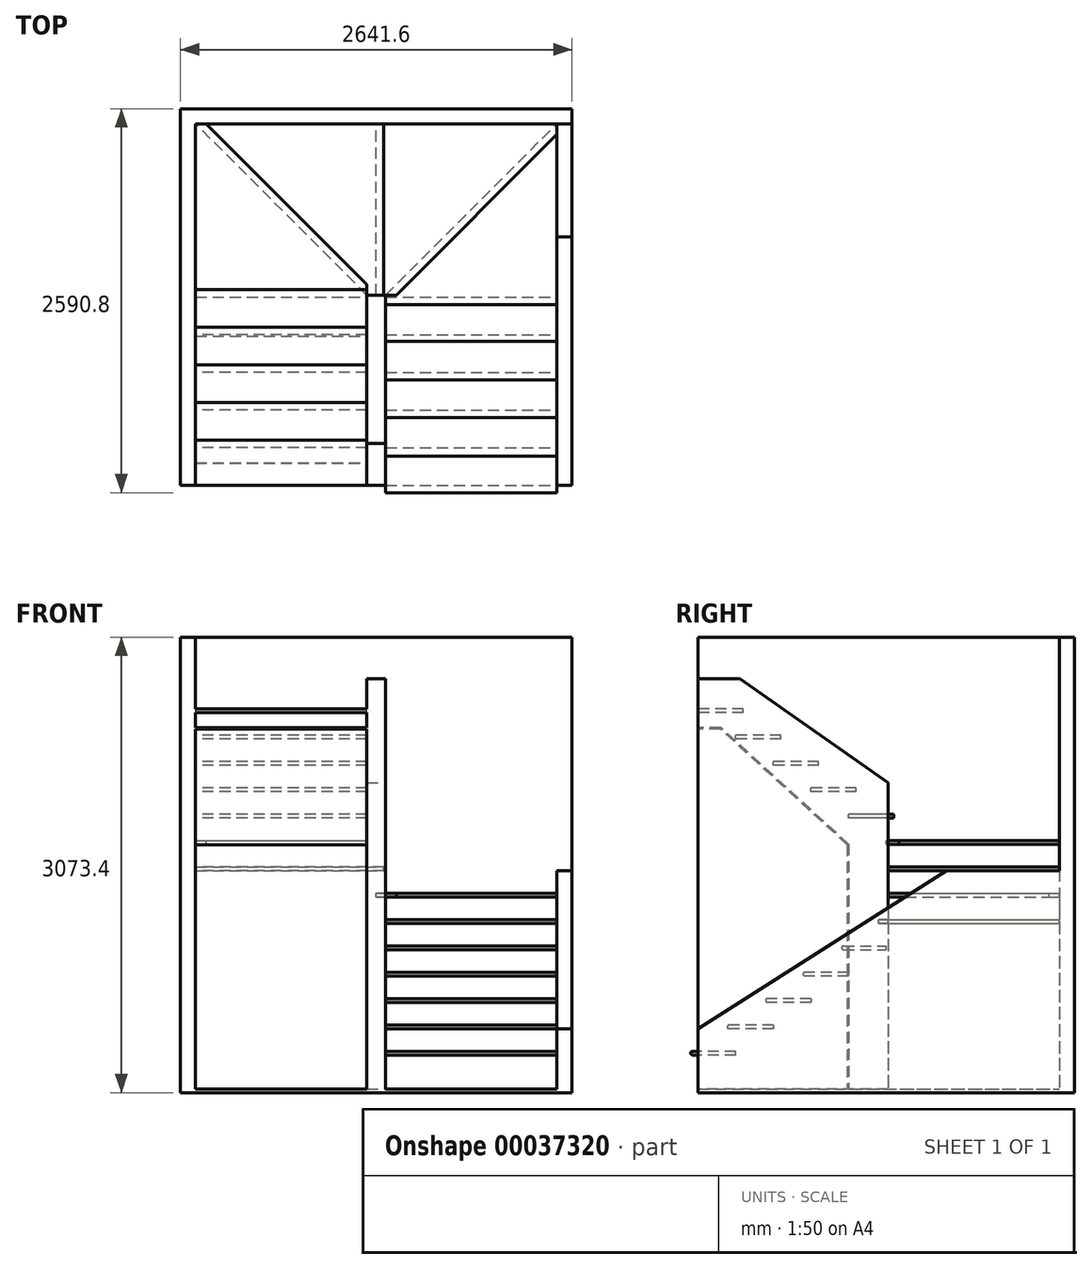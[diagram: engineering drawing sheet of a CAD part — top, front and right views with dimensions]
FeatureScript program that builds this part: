
annotation { "Feature Type Name" : "Feature", "Feature Type Description" : "" }
export const myFeature = defineFeature(function(context is Context, id is Id, definition is map)
    precondition{}
    {
        {
            var Q0;
            Q0=qCreatedBy(makeId("Top.planeOp"),FACE);
            var sketch = newSketch(context, id + "F0", { "sketchPlane" : qUnion([Q0])});
            skLineSegment(sketch, "E0.bottom", {"start": v(-1219.2, 0) * mm, "end": v(-63.5, 0) * mm});
            skLineSegment(sketch, "E0.top", {"start": v(-1219.2, 2438.4) * mm, "end": v(1219.2, 2438.4) * mm});
            skLineSegment(sketch, "E0.left", {"start": v(-1219.2, 0) * mm, "end": v(-1219.2, 2438.4) * mm});
            skLineSegment(sketch, "E0.right", {"start": v(1219.2, 0) * mm, "end": v(1219.2, 2438.4) * mm});
            skLineSegment(sketch, "E1", {"start": v(-63.5, 0) * mm, "end": v(-63.5, 1282.7) * mm});
            skLineSegment(sketch, "E2", {"start": v(-63.5, 1282.7) * mm, "end": v(63.5, 1282.7) * mm});
            skLineSegment(sketch, "E3", {"start": v(63.5, 1282.7) * mm, "end": v(63.5, 0) * mm});
            skLineSegment(sketch, "E4", {"start": v(0, 1282.7) * mm, "end": v(0, 0) * mm, "construction": true});
            skLineSegment(sketch, "E5.trimOffspring", {"start": v(63.5, 0) * mm, "end": v(1219.2, 0) * mm});
            skLineSegment(sketch, "E6", {"start": v(-1219.2, 254) * mm, "end": v(-63.5, 254) * mm});
            skLineSegment(sketch, "E7", {"start": v(-1219.2, 508) * mm, "end": v(-63.5, 508) * mm});
            skLineSegment(sketch, "E8", {"start": v(-1219.2, 762) * mm, "end": v(-63.5, 762) * mm});
            skLineSegment(sketch, "E9", {"start": v(-1219.2, 1016) * mm, "end": v(-63.5, 1016) * mm});
            skLineSegment(sketch, "E10", {"start": v(0, 1282.7) * mm, "end": v(0, 2438.4) * mm});
            skLineSegment(sketch, "E11", {"start": v(63.5, 1282.7) * mm, "end": v(1219.2, 2438.4) * mm});
            skLineSegment(sketch, "E12", {"start": v(-63.5, 1282.7) * mm, "end": v(-1219.2, 2438.4) * mm});
            skLineSegment(sketch, "E13.trimOffspring", {"start": v(63.5, 762) * mm, "end": v(1219.2, 762) * mm});
            skLineSegment(sketch, "E14.trimOffspring", {"start": v(63.5, 508) * mm, "end": v(1219.2, 508) * mm});
            skLineSegment(sketch, "E15.trimOffspring", {"start": v(63.5, 254) * mm, "end": v(1219.2, 254) * mm});
            skLineSegment(sketch, "E16.trimOffspring", {"start": v(63.5, 1016) * mm, "end": v(1219.2, 1016) * mm});
            skLineSegment(sketch, "E17", {"start": v(-1219.2, 1270) * mm, "end": v(-63.5, 1270) * mm});
            skLineSegment(sketch, "E18.trimOffspring", {"start": v(63.5, 1270) * mm, "end": v(1219.2, 1270) * mm});
            skSolve(sketch);
        }
        {
            var Q0;
            Q0=qCreatedBy(makeId("Top.planeOp"),FACE);
            var sketch = newSketch(context, id + "F1", { "sketchPlane" : qUnion([Q0])});
            skLineSegment(sketch, "E19.0", {"start": v(-1219.2, 0) * mm, "end": v(-1219.2, 2438.4) * mm});
            skLineSegment(sketch, "E19.1", {"start": v(-1219.2, 2438.4) * mm, "end": v(1219.2, 2438.4) * mm});
            skLineSegment(sketch, "E19.2", {"start": v(1219.2, 0) * mm, "end": v(1219.2, 2438.4) * mm});
            skLineSegment(sketch, "E20.0", {"start": v(1320.8, 0) * mm, "end": v(1320.8, 2540) * mm});
            skLineSegment(sketch, "E20.1", {"start": v(-1320.8, 2540) * mm, "end": v(1320.8, 2540) * mm});
            skLineSegment(sketch, "E20.2", {"start": v(-1320.8, 0) * mm, "end": v(-1320.8, 2540) * mm});
            skLineSegment(sketch, "E21", {"start": v(-1320.8, 0) * mm, "end": v(-1219.2, 0) * mm});
            skLineSegment(sketch, "E22", {"start": v(1219.2, 0) * mm, "end": v(1320.8, 0) * mm});
            skSolve(sketch);
        }
        {
            var Q0;
            Q0 = qSketchRegion(id + "F1", true);
            extrude(context, id + "F2", {"entities" : qUnion([Q0]), "depth" : 3048 * mm});
        }
        {
            var Q0;
            Q0=qCreatedBy(makeId("Top.planeOp"),FACE);
            cPlane(context, id + "F3", {"entities" : qUnion([Q0]), "cplaneType" : CPlaneType.OFFSET, "offset" : 254 * mm, "width" : 152.4 * mm, "height" : 152.4 * mm});
        }
        {
            var Q0;
            Q0=qCreatedBy(id+"F3.planeOp",FACE);
            var sketch = newSketch(context, id + "F4", { "sketchPlane" : qUnion([Q0])});
            skLineSegment(sketch, "E23.bottom", {"start": v(63.5, 254) * mm, "end": v(1219.2, 254) * mm});
            skLineSegment(sketch, "E23.top", {"start": v(63.5, -50.8) * mm, "end": v(1219.2, -50.8) * mm});
            skLineSegment(sketch, "E23.left", {"start": v(63.5, 254) * mm, "end": v(63.5, -50.8) * mm});
            skLineSegment(sketch, "E23.right", {"start": v(1219.2, 254) * mm, "end": v(1219.2, -50.8) * mm});
            skSolve(sketch);
        }
        {
            var Q0;
            Q0 = qSketchRegion(id + "F4", true);
            extrude(context, id + "F5", {"entities" : qUnion([Q0]), "operationType" : NewBodyOperationType.ADD, "oppositeDirection" : true, "depth" : 25.4 * mm});
        }
        {
            var Q0;
            Q0=makeQuery(id+"F5.opExtrude","CAP_EDGE",EDGE,{"disambiguationData":[OSD([sQuery(id+"F4.wireOp",EDGE,"E23.top")])],"isStart":true});
            var Q1;
            Q1=makeQuery(id+"F5.opExtrude","CAP_EDGE",EDGE,{"disambiguationData":[OSD([sQuery(id+"F4.wireOp",EDGE,"E23.top")])],"isStart":false});
            fillet(context, id + "F6", {"entities" : qUnion([Q0, Q1]), "radius" : 12.7 * mm, "tangentPropagation" : true, "allowEdgeOverflow" : false});
        }
        {
            var Q0;
            Q0=makeQuery(id+"F2.opExtrude","SWEPT_FACE",FACE,{"disambiguationData":[OSD([sQuery(id+"F1.wireOp",EDGE,"E19.2")])]});
            var sketch = newSketch(context, id + "F7", { "sketchPlane" : qUnion([Q0])});
            skLineSegment(sketch, "E24", {"start": v(-254, 0) * mm, "end": v(-254, 431.8) * mm, "construction": true});
            skLineSegment(sketch, "E25", {"start": v(-254, 431.8) * mm, "end": v(-508, 431.8) * mm, "construction": true});
            skLineSegment(sketch, "E26", {"start": v(-508, 431.8) * mm, "end": v(-508, 609.6) * mm, "construction": true});
            skLineSegment(sketch, "E27", {"start": v(-508, 609.6) * mm, "end": v(-762, 609.6) * mm, "construction": true});
            skLineSegment(sketch, "E28", {"start": v(-762, 609.6) * mm, "end": v(-762, 787.4) * mm, "construction": true});
            skLineSegment(sketch, "E29", {"start": v(-762, 787.4) * mm, "end": v(-1016, 787.4) * mm, "construction": true});
            skLineSegment(sketch, "E30", {"start": v(-1016, 787.4) * mm, "end": v(-1016, 2232.09) * mm, "construction": true});
            skLineSegment(sketch, "E31.bottom", {"start": v(-1016, 787.4) * mm, "end": v(-717.55, 787.4) * mm});
            skLineSegment(sketch, "E31.top", {"start": v(-1016, 762) * mm, "end": v(-717.55, 762) * mm});
            skLineSegment(sketch, "E31.left", {"start": v(-1016, 762) * mm, "end": v(-1016, 787.4) * mm});
            skLineSegment(sketch, "E31.right", {"start": v(-711.2, 768.35) * mm, "end": v(-711.2, 781.05) * mm});
            skLineSegment(sketch, "E32.bottom", {"start": v(-762, 609.6) * mm, "end": v(-463.55, 609.6) * mm});
            skLineSegment(sketch, "E32.top", {"start": v(-762, 584.2) * mm, "end": v(-463.55, 584.2) * mm});
            skLineSegment(sketch, "E32.left", {"start": v(-762, 609.6) * mm, "end": v(-762, 584.2) * mm});
            skLineSegment(sketch, "E32.right", {"start": v(-457.2, 603.25) * mm, "end": v(-457.2, 590.55) * mm});
            skLineSegment(sketch, "E33.bottom", {"start": v(-508, 431.8) * mm, "end": v(-209.55, 431.8) * mm});
            skLineSegment(sketch, "E33.top", {"start": v(-508, 406.4) * mm, "end": v(-203.2, 406.4) * mm});
            skLineSegment(sketch, "E33.left", {"start": v(-508, 431.8) * mm, "end": v(-508, 406.4) * mm});
            skLineSegment(sketch, "E33.right", {"start": v(-196.85, 419.1) * mm, "end": v(-196.85, 412.75) * mm});
            skPoint(sketch, "E34.visualSharp", {"position": v(-711.2, 787.4) * mm});
            skArc(sketch, "E34.filletArc", {"start": v(-711.2, 781.05) * mm, "mid": v(-713.06, 785.54) * mm, "end": v(-717.55, 787.4) * mm});
            skPoint(sketch, "E35.visualSharp", {"position": v(-711.2, 762) * mm});
            skArc(sketch, "E35.filletArc", {"start": v(-717.55, 762) * mm, "mid": v(-713.06, 763.86) * mm, "end": v(-711.2, 768.35) * mm});
            skPoint(sketch, "E36.visualSharp", {"position": v(-457.2, 609.6) * mm});
            skArc(sketch, "E36.filletArc", {"start": v(-457.2, 603.25) * mm, "mid": v(-459.06, 607.74) * mm, "end": v(-463.55, 609.6) * mm});
            skPoint(sketch, "E37.visualSharp", {"position": v(-457.2, 584.2) * mm});
            skArc(sketch, "E37.filletArc", {"start": v(-463.55, 584.2) * mm, "mid": v(-459.06, 586.06) * mm, "end": v(-457.2, 590.55) * mm});
            skPoint(sketch, "E38.visualSharp", {"position": v(-196.85, 406.4) * mm});
            skArc(sketch, "E38.filletArc", {"start": v(-203.2, 406.4) * mm, "mid": v(-198.7, 408.26) * mm, "end": v(-196.85, 412.75) * mm});
            skPoint(sketch, "E39.visualSharp", {"position": v(-196.85, 431.8) * mm});
            skArc(sketch, "E39.filletArc", {"start": v(-196.85, 419.1) * mm, "mid": v(-200.57, 428.08) * mm, "end": v(-209.55, 431.8) * mm});
            skLineSegment(sketch, "E40.bottom", {"start": v(-977.9, 939.8) * mm, "end": v(-1270, 939.8) * mm});
            skLineSegment(sketch, "E40.top", {"start": v(-977.9, 965.2) * mm, "end": v(-1270, 965.2) * mm});
            skLineSegment(sketch, "E40.left", {"start": v(-971.55, 946.15) * mm, "end": v(-971.55, 958.85) * mm});
            skLineSegment(sketch, "E40.right", {"start": v(-1270, 939.8) * mm, "end": v(-1270, 965.2) * mm});
            skPoint(sketch, "E41.visualSharp", {"position": v(-971.55, 965.2) * mm});
            skArc(sketch, "E41.filletArc", {"start": v(-971.55, 958.85) * mm, "mid": v(-973.4, 963.34) * mm, "end": v(-977.9, 965.2) * mm});
            skPoint(sketch, "E42.visualSharp", {"position": v(-971.55, 939.8) * mm});
            skArc(sketch, "E42.filletArc", {"start": v(-977.9, 939.8) * mm, "mid": v(-973.4, 941.66) * mm, "end": v(-971.55, 946.15) * mm});
            skSolve(sketch);
        }
        {
            var Q0;
            Q0 = qSketchRegion(id + "F7", true);
            var Q1;
            Q1=makeQuery(id+"F5.opExtrude","SWEPT_FACE",FACE,{"disambiguationData":[OSD([sQuery(id+"F4.wireOp",EDGE,"E23.left")])]});
            extrude(context, id + "F8", {"entities" : qUnion([Q0]), "operationType" : NewBodyOperationType.ADD, "endBound" : BoundingType.UP_TO_SURFACE, "endBoundEntityFace" : qUnion([Q1]), "depth" : 25.4 * mm});
        }
        {
            var Q0;
            Q0=makeQuery(id+"F8.opExtrude","SWEPT_FACE",FACE,{"disambiguationData":[OSD([sQuery(id+"F7.wireOp",EDGE,"E31.bottom")])]});
            cPlane(context, id + "F9", {"entities" : qUnion([Q0]), "cplaneType" : CPlaneType.OFFSET, "offset" : 355.6 * mm, "width" : 152.4 * mm, "height" : 152.4 * mm});
        }
        {
            var Q0;
            Q0=qCreatedBy(id+"F9.planeOp",FACE);
            var sketch = newSketch(context, id + "F10", { "sketchPlane" : qUnion([Q0])});
            skLineSegment(sketch, "E43.0", {"start": v(63.5, 1282.7) * mm, "end": v(1219.2, 2438.4) * mm});
            skLineSegment(sketch, "E44", {"start": v(63.5, 1282.7) * mm, "end": v(63.5, 1219.2) * mm});
            skLineSegment(sketch, "E45", {"start": v(63.5, 1219.2) * mm, "end": v(1219.2, 1219.2) * mm});
            skLineSegment(sketch, "E46", {"start": v(1219.2, 1219.2) * mm, "end": v(1219.2, 2438.4) * mm});
            skSolve(sketch);
        }
        {
            var Q0;
            Q0 = qSketchRegion(id + "F10", true);
            extrude(context, id + "F11", {"entities" : qUnion([Q0]), "operationType" : NewBodyOperationType.ADD, "oppositeDirection" : true, "depth" : 25.4 * mm});
        }
        {
            var Q0;
            Q0=qCreatedBy(id+"F9.planeOp",FACE);
            cPlane(context, id + "F12", {"entities" : qUnion([Q0]), "cplaneType" : CPlaneType.OFFSET, "offset" : 177.8 * mm, "width" : 152.4 * mm, "height" : 152.4 * mm});
        }
        {
            var Q0;
            Q0=qCreatedBy(id+"F12.planeOp",FACE);
            var sketch = newSketch(context, id + "F13", { "sketchPlane" : qUnion([Q0])});
            skLineSegment(sketch, "E47.0", {"start": v(0, 1282.7) * mm, "end": v(0, 2438.4) * mm});
            skLineSegment(sketch, "E48", {"start": v(0, 1282.7) * mm, "end": v(135.34, 1282.7) * mm});
            skLineSegment(sketch, "E49", {"start": v(135.34, 1282.7) * mm, "end": v(1219.2, 2366.56) * mm});
            skLineSegment(sketch, "E50", {"start": v(1219.2, 2366.56) * mm, "end": v(1219.2, 2438.4) * mm});
            skLineSegment(sketch, "E51", {"start": v(1219.2, 2438.4) * mm, "end": v(0, 2438.4) * mm});
            skSolve(sketch);
        }
        {
            var Q0;
            Q0 = qSketchRegion(id + "F13", true);
            extrude(context, id + "F14", {"entities" : qUnion([Q0]), "operationType" : NewBodyOperationType.ADD, "oppositeDirection" : true, "depth" : 25.4 * mm});
        }
        {
            var Q0;
            Q0=qCreatedBy(id+"F12.planeOp",FACE);
            cPlane(context, id + "F15", {"entities" : qUnion([Q0]), "cplaneType" : CPlaneType.OFFSET, "offset" : 177.8 * mm, "width" : 152.4 * mm, "height" : 152.4 * mm});
        }
        {
            var Q0;
            Q0=qCreatedBy(id+"F15.planeOp",FACE);
            var sketch = newSketch(context, id + "F16", { "sketchPlane" : qUnion([Q0])});
            skLineSegment(sketch, "E52.0", {"start": v(-63.5, 1282.7) * mm, "end": v(-1219.2, 2438.4) * mm});
            skLineSegment(sketch, "E53", {"start": v(-1219.2, 2438.4) * mm, "end": v(50.8, 2438.4) * mm});
            skLineSegment(sketch, "E54", {"start": v(50.8, 2438.4) * mm, "end": v(50.8, 1282.7) * mm});
            skLineSegment(sketch, "E55", {"start": v(50.8, 1282.7) * mm, "end": v(-63.5, 1282.7) * mm});
            skSolve(sketch);
        }
        {
            var Q0;
            Q0 = qSketchRegion(id + "F16", true);
            extrude(context, id + "F17", {"entities" : qUnion([Q0]), "operationType" : NewBodyOperationType.ADD, "oppositeDirection" : true, "depth" : 25.4 * mm});
        }
        {
            var Q0;
            Q0=makeQuery(id+"F17.opExtrude","CAP_FACE",FACE,{"disambiguationData":[OSD([sQuery(id+"F16.wireOp",EDGE,"E52.0"),sQuery(id+"F16.wireOp",EDGE,"E53"),sQuery(id+"F16.wireOp",EDGE,"E54"),sQuery(id+"F16.wireOp",EDGE,"E55")])],"isStart":true});
            cPlane(context, id + "F18", {"entities" : qUnion([Q0]), "cplaneType" : CPlaneType.OFFSET, "offset" : 177.8 * mm, "width" : 152.4 * mm, "height" : 152.4 * mm});
        }
        {
            var Q0;
            Q0=qCreatedBy(id+"F18.planeOp",FACE);
            var sketch = newSketch(context, id + "F19", { "sketchPlane" : qUnion([Q0])});
            skLineSegment(sketch, "E56.0", {"start": v(-1219.2, 1270) * mm, "end": v(-63.5, 1270) * mm});
            skLineSegment(sketch, "E57", {"start": v(-1219.2, 1270) * mm, "end": v(-1219.2, 2438.4) * mm});
            skLineSegment(sketch, "E58", {"start": v(-1219.2, 2438.4) * mm, "end": v(-1147.36, 2438.4) * mm});
            skLineSegment(sketch, "E59", {"start": v(-1147.36, 2438.4) * mm, "end": v(-63.5, 1354.54) * mm});
            skLineSegment(sketch, "E60", {"start": v(-63.5, 1354.54) * mm, "end": v(-63.5, 1270) * mm});
            skSolve(sketch);
        }
        {
            var Q0;
            Q0 = qSketchRegion(id + "F19", true);
            extrude(context, id + "F20", {"entities" : qUnion([Q0]), "operationType" : NewBodyOperationType.ADD, "oppositeDirection" : true, "depth" : 25.4 * mm});
        }
        {
            var Q0;
            Q0=makeQuery(id+"F2.opExtrude","SWEPT_FACE",FACE,{"disambiguationData":[OSD([sQuery(id+"F1.wireOp",EDGE,"E19.0")])]});
            var sketch = newSketch(context, id + "F21", { "sketchPlane" : qUnion([Q0])});
            skLineSegment(sketch, "E61.bottom", {"start": v(1320.8, 1828.8) * mm, "end": v(1016, 1828.8) * mm});
            skLineSegment(sketch, "E61.top", {"start": v(1320.8, 1854.2) * mm, "end": v(1016, 1854.2) * mm});
            skLineSegment(sketch, "E61.left", {"start": v(1320.8, 1828.8) * mm, "end": v(1320.8, 1854.2) * mm});
            skLineSegment(sketch, "E61.right", {"start": v(1016, 1828.8) * mm, "end": v(1016, 1854.2) * mm});
            skLineSegment(sketch, "E62.bottom", {"start": v(1066.8, 2006.6) * mm, "end": v(762, 2006.6) * mm});
            skLineSegment(sketch, "E62.top", {"start": v(1066.8, 2032) * mm, "end": v(762, 2032) * mm});
            skLineSegment(sketch, "E62.left", {"start": v(1066.8, 2006.6) * mm, "end": v(1066.8, 2032) * mm});
            skLineSegment(sketch, "E62.right", {"start": v(762, 2006.6) * mm, "end": v(762, 2032) * mm});
            skLineSegment(sketch, "E63.bottom", {"start": v(812.8, 2184.4) * mm, "end": v(508, 2184.4) * mm});
            skLineSegment(sketch, "E63.top", {"start": v(812.8, 2209.8) * mm, "end": v(508, 2209.8) * mm});
            skLineSegment(sketch, "E63.left", {"start": v(812.8, 2184.4) * mm, "end": v(812.8, 2209.8) * mm});
            skLineSegment(sketch, "E63.right", {"start": v(508, 2184.4) * mm, "end": v(508, 2209.8) * mm});
            skLineSegment(sketch, "E64.bottom", {"start": v(558.8, 2362.2) * mm, "end": v(254, 2362.2) * mm});
            skLineSegment(sketch, "E64.top", {"start": v(558.8, 2387.6) * mm, "end": v(254, 2387.6) * mm});
            skLineSegment(sketch, "E64.left", {"start": v(558.8, 2362.2) * mm, "end": v(558.8, 2387.6) * mm});
            skLineSegment(sketch, "E64.right", {"start": v(254, 2362.2) * mm, "end": v(254, 2387.6) * mm});
            skLineSegment(sketch, "E65.bottom", {"start": v(304.8, 2540) * mm, "end": v(0, 2540) * mm});
            skLineSegment(sketch, "E65.top", {"start": v(304.8, 2565.4) * mm, "end": v(0, 2565.4) * mm});
            skLineSegment(sketch, "E65.left", {"start": v(304.8, 2540) * mm, "end": v(304.8, 2565.4) * mm});
            skLineSegment(sketch, "E65.right", {"start": v(0, 2540) * mm, "end": v(0, 2565.4) * mm});
            skLineSegment(sketch, "E66", {"start": v(1270, 1676.4) * mm, "end": v(1270, 2025.36) * mm, "construction": true});
            skSolve(sketch);
        }
        {
            var Q0;
            Q0 = qSketchRegion(id + "F21", true);
            extrude(context, id + "F22", {"entities" : qUnion([Q0]), "operationType" : NewBodyOperationType.ADD, "depth" : 1155.7 * mm});
        }
        {
            var Q0;
            Q0=qCreatedBy(makeId("Top.planeOp"),FACE);
            var sketch = newSketch(context, id + "F23", { "sketchPlane" : qUnion([Q0])});
            skLineSegment(sketch, "E67.bottom", {"start": v(-63.5, 1282.7) * mm, "end": v(63.5, 1282.7) * mm});
            skLineSegment(sketch, "E67.top", {"start": v(-63.5, 0) * mm, "end": v(63.5, 0) * mm});
            skLineSegment(sketch, "E67.left", {"start": v(-63.5, 1282.7) * mm, "end": v(-63.5, 0) * mm});
            skLineSegment(sketch, "E67.right", {"start": v(63.5, 1282.7) * mm, "end": v(63.5, 0) * mm});
            skSolve(sketch);
        }
        {
            var Q0;
            Q0=makeQuery(id+"F2.opExtrude","CAP_FACE",FACE,{"disambiguationData":[OSD([sQuery(id+"F1.wireOp",EDGE,"E19.0"),sQuery(id+"F1.wireOp",EDGE,"E19.1"),sQuery(id+"F1.wireOp",EDGE,"E19.2"),sQuery(id+"F1.wireOp",EDGE,"E20.0"),sQuery(id+"F1.wireOp",EDGE,"E20.1"),sQuery(id+"F1.wireOp",EDGE,"E20.2"),sQuery(id+"F1.wireOp",EDGE,"E21"),sQuery(id+"F1.wireOp",EDGE,"E22")])],"isStart":true});
            var sketch = newSketch(context, id + "F24", { "sketchPlane" : qUnion([Q0])});
            skLineSegment(sketch, "E68.bottom", {"start": v(-1320.8, -2540) * mm, "end": v(1320.8, -2540) * mm});
            skLineSegment(sketch, "E68.top", {"start": v(-1320.8, 0) * mm, "end": v(1320.8, 0) * mm});
            skLineSegment(sketch, "E68.left", {"start": v(-1320.8, -2540) * mm, "end": v(-1320.8, 0) * mm});
            skLineSegment(sketch, "E68.right", {"start": v(1320.8, -2540) * mm, "end": v(1320.8, 0) * mm});
            skSolve(sketch);
        }
        {
            var Q0;
            Q0 = qSketchRegion(id + "F24", true);
            extrude(context, id + "F25", {"entities" : qUnion([Q0]), "operationType" : NewBodyOperationType.ADD, "depth" : 25.4 * mm});
        }
        {
            var Q0;
            Q0 = qSketchRegion(id + "F23", true);
            extrude(context, id + "F26", {"entities" : qUnion([Q0]), "operationType" : NewBodyOperationType.ADD, "depth" : 2768.6 * mm});
        }
        {
            var Q0;
            Q0=makeQuery(id+"F2.opExtrude","SWEPT_FACE",FACE,{"disambiguationData":[OSD([sQuery(id+"F1.wireOp",EDGE,"E19.2")])]});
            var sketch = newSketch(context, id + "F27", { "sketchPlane" : qUnion([Q0])});
            skLineSegment(sketch, "E69", {"start": v(0, 406.4) * mm, "end": v(-1676.4, 1473.2) * mm});
            skLineSegment(sketch, "E70", {"start": v(-1676.4, 1473.2) * mm, "end": v(-2438.4, 1473.2) * mm});
            skSolve(sketch);
        }
        {
            var Q0;
            Q0 = qSketchRegion(id + "F27", true);
            var Q1;
            {var subQ10=sQuery(id+"F27.wireOp",EDGE,"E69");Q1=makeQuery(id+"F27.imprint","IMPRINT",FACE,{"disambiguationData":[TD([[makeQuery(id+"F27.imprint","IMPRINT",EDGE,{"derivedFrom":subQ10}),-1.0]])]});}
            extrude(context, id + "F28", {"entities" : qUnion([Q0, Q1]), "operationType" : NewBodyOperationType.REMOVE, "endBound" : BoundingType.THROUGH_ALL, "oppositeDirection" : true, "depth" : 25.4 * mm});
        }
        {
            var Q0;
            Q0=makeQuery(id+"F26.opExtrude","SWEPT_FACE",FACE,{"disambiguationData":[OSD([sQuery(id+"F23.wireOp",EDGE,"E67.right")])]});
            var sketch = newSketch(context, id + "F29", { "sketchPlane" : qUnion([Q0])});
            skLineSegment(sketch, "E71", {"start": v(280.27, 2768.6) * mm, "end": v(1282.7, 2066.9) * mm});
            skLineSegment(sketch, "E72", {"start": v(-586.35, 3189.2) * mm, "end": v(1282.7, 1880.87) * mm, "construction": true});
            skPoint(sketch, "E73", {"position": v(304.8, 2565.4) * mm});
            skPoint(sketch, "E74", {"position": v(1066.8, 2032) * mm});
            skLineSegment(sketch, "E75", {"start": v(280.27, 2768.6) * mm, "end": v(1282.7, 2768.6) * mm});
            skLineSegment(sketch, "E76", {"start": v(1282.7, 2768.6) * mm, "end": v(1282.7, 2066.9) * mm});
            skSolve(sketch);
        }
        {
            var Q0;
            Q0 = qSketchRegion(id + "F29", true);
            extrude(context, id + "F30", {"entities" : qUnion([Q0]), "operationType" : NewBodyOperationType.REMOVE, "oppositeDirection" : true, "depth" : 152.4 * mm});
        }
        {
            var Q0;
            Q0=makeQuery(id+"F26.opExtrude","SWEPT_FACE",FACE,{"disambiguationData":[OSD([sQuery(id+"F23.wireOp",EDGE,"E67.left")])]});
            var sketch = newSketch(context, id + "F31", { "sketchPlane" : qUnion([Q0])});
            skLineSegment(sketch, "E77", {"start": v(-1016, 1651) * mm, "end": v(-152.4, 2438.4) * mm});
            skLineSegment(sketch, "E78", {"start": v(-152.4, 2438.4) * mm, "end": v(0, 2438.4) * mm});
            skLineSegment(sketch, "E79", {"start": v(-1016, 1651) * mm, "end": v(-1016, 0) * mm});
            skLineSegment(sketch, "E80.0", {"start": v(-1006.48, 1646.8) * mm, "end": v(-1006.48, 0) * mm});
            skLineSegment(sketch, "E80.1", {"start": v(-1006.48, 1646.8) * mm, "end": v(-148.7, 2428.88) * mm});
            skLineSegment(sketch, "E80.2", {"start": v(-148.7, 2428.88) * mm, "end": v(0, 2428.88) * mm});
            skLineSegment(sketch, "E81", {"start": v(-1016, 0) * mm, "end": v(-1006.48, 0) * mm});
            skLineSegment(sketch, "E82", {"start": v(0, 2438.4) * mm, "end": v(0, 2428.88) * mm});
            skSolve(sketch);
        }
        {
            var Q0;
            Q0 = qSketchRegion(id + "F31", true);
            extrude(context, id + "F32", {"entities" : qUnion([Q0]), "operationType" : NewBodyOperationType.ADD, "endBound" : BoundingType.UP_TO_NEXT, "depth" : 25.4 * mm});
        }
    });
